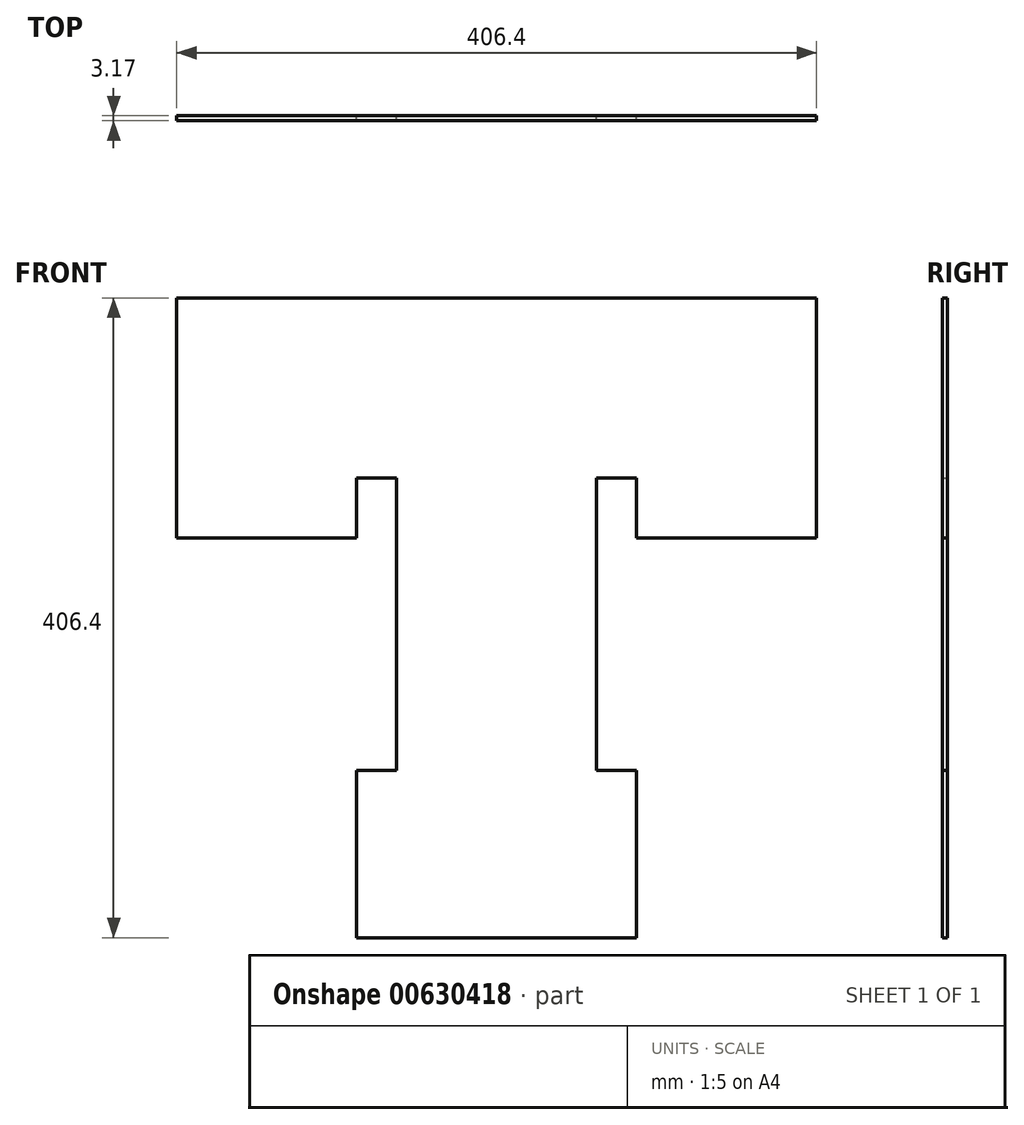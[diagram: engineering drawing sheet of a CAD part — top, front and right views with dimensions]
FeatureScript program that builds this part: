
annotation { "Feature Type Name" : "Feature", "Feature Type Description" : "" }
export const myFeature = defineFeature(function(context is Context, id is Id, definition is map)
    precondition{}
    {
        {
            var Q0;
            Q0=qCreatedBy(makeId("Front.planeOp"),FACE);
            var sketch = newSketch(context, id + "F0", { "sketchPlane" : qUnion([Q0])});
            skLineSegment(sketch, "E0.bottom", {"start": v(-25.4, 330.2) * mm, "end": v(0, 330.2) * mm});
            skLineSegment(sketch, "E0.top", {"start": v(-25.4, 0) * mm, "end": v(0, 0) * mm});
            skLineSegment(sketch, "E0.left", {"start": v(-25.4, 292.1) * mm, "end": v(-25.4, 30.02) * mm, "construction": true});
            skLineSegment(sketch, "E0.right", {"start": v(0, 330.2) * mm, "end": v(0, 0) * mm, "construction": true});
            skLineSegment(sketch, "E1.bottom", {"start": v(0, 330.2) * mm, "end": v(-165.1, 330.2) * mm, "construction": true});
            skLineSegment(sketch, "E1.top", {"start": v(-25.4, 292.1) * mm, "end": v(-127, 292.1) * mm, "construction": true});
            skLineSegment(sketch, "E1.left", {"start": v(0, 330.2) * mm, "end": v(0, 292.1) * mm});
            skLineSegment(sketch, "E1.right", {"start": v(-165.1, 330.2) * mm, "end": v(-165.1, 292.1) * mm});
            skLineSegment(sketch, "E2.bottom", {"start": v(-165.1, 330.2) * mm, "end": v(-127, 330.2) * mm, "construction": true});
            skLineSegment(sketch, "E2.top", {"start": v(-165.1, 254) * mm, "end": v(-127, 254) * mm, "construction": true});
            skLineSegment(sketch, "E2.left", {"start": v(-165.1, 330.2) * mm, "end": v(-165.1, 254) * mm, "construction": true});
            skLineSegment(sketch, "E2.right", {"start": v(-127, 292.1) * mm, "end": v(-127, 254) * mm, "construction": true});
            skLineSegment(sketch, "E3.bottom", {"start": v(0, 0) * mm, "end": v(-50.8, 0) * mm, "construction": true});
            skLineSegment(sketch, "E3.top", {"start": v(-25.4, 30.02) * mm, "end": v(-50.8, 30.02) * mm, "construction": true});
            skLineSegment(sketch, "E3.left", {"start": v(0, 0) * mm, "end": v(0, 30.02) * mm});
            skLineSegment(sketch, "E3.right", {"start": v(-50.8, 0) * mm, "end": v(-50.8, 30.02) * mm, "construction": true});
            skLineSegment(sketch, "E4.MirrorCS", {"start": v(0, 330.2) * mm, "end": v(165.1, 330.2) * mm, "construction": true});
            skLineSegment(sketch, "E5.MirrorCS", {"start": v(165.1, 330.2) * mm, "end": v(165.1, 254) * mm, "construction": true});
            skLineSegment(sketch, "E6.MirrorCS", {"start": v(165.1, 254) * mm, "end": v(127, 254) * mm, "construction": true});
            skLineSegment(sketch, "E7.MirrorCS", {"start": v(127, 292.1) * mm, "end": v(127, 254) * mm, "construction": true});
            skLineSegment(sketch, "E8.MirrorCS", {"start": v(25.4, 292.1) * mm, "end": v(127, 292.1) * mm, "construction": true});
            skLineSegment(sketch, "E9.MirrorCS", {"start": v(25.4, 292.1) * mm, "end": v(25.4, 30.02) * mm, "construction": true});
            skLineSegment(sketch, "E10.MirrorCS", {"start": v(25.4, 30.02) * mm, "end": v(50.8, 30.02) * mm, "construction": true});
            skLineSegment(sketch, "E11.MirrorCS", {"start": v(50.8, 0) * mm, "end": v(50.8, 30.02) * mm, "construction": true});
            skLineSegment(sketch, "E12.MirrorCS", {"start": v(0, 0) * mm, "end": v(50.8, 0) * mm, "construction": true});
            skLineSegment(sketch, "E13.0", {"start": v(-63.5, 254) * mm, "end": v(-88.9, 254) * mm});
            skLineSegment(sketch, "E13.1", {"start": v(-88.9, 254) * mm, "end": v(-88.9, 215.9) * mm});
            skLineSegment(sketch, "E13.2", {"start": v(-203.2, 215.9) * mm, "end": v(-88.9, 215.9) * mm});
            skLineSegment(sketch, "E13.3", {"start": v(-203.2, 368.3) * mm, "end": v(-203.2, 215.9) * mm});
            skLineSegment(sketch, "E13.4", {"start": v(0, 368.3) * mm, "end": v(-203.2, 368.3) * mm});
            skLineSegment(sketch, "E13.5", {"start": v(-63.5, 254) * mm, "end": v(-63.5, 68.12) * mm});
            skLineSegment(sketch, "E13.6", {"start": v(0, 368.3) * mm, "end": v(203.2, 368.3) * mm});
            skLineSegment(sketch, "E13.7", {"start": v(203.2, 368.3) * mm, "end": v(203.2, 215.9) * mm});
            skLineSegment(sketch, "E13.8", {"start": v(0, -38.1) * mm, "end": v(88.9, -38.1) * mm});
            skLineSegment(sketch, "E13.9", {"start": v(0, -38.1) * mm, "end": v(-88.9, -38.1) * mm});
            skLineSegment(sketch, "E13.10", {"start": v(-88.9, -38.1) * mm, "end": v(-88.9, 68.12) * mm});
            skLineSegment(sketch, "E13.11", {"start": v(-63.5, 68.12) * mm, "end": v(-88.9, 68.12) * mm});
            skLineSegment(sketch, "E13.12", {"start": v(88.9, -38.1) * mm, "end": v(88.9, 68.12) * mm});
            skLineSegment(sketch, "E13.13", {"start": v(63.5, 68.12) * mm, "end": v(88.9, 68.12) * mm});
            skLineSegment(sketch, "E13.14", {"start": v(63.5, 254) * mm, "end": v(63.5, 68.12) * mm});
            skLineSegment(sketch, "E13.15", {"start": v(63.5, 254) * mm, "end": v(88.9, 254) * mm});
            skLineSegment(sketch, "E13.16", {"start": v(88.9, 254) * mm, "end": v(88.9, 215.9) * mm});
            skLineSegment(sketch, "E13.17", {"start": v(203.2, 215.9) * mm, "end": v(88.9, 215.9) * mm});
            skSolve(sketch);
        }
        {
            var Q0;
            Q0=qSketchRegion(id+"F0",true);
            extrude(context, id + "F1", {"entities" : qUnion([Q0]), "depth" : 3.17 * mm, "offsetDistance" : 25.4 * mm});
        }
    });
